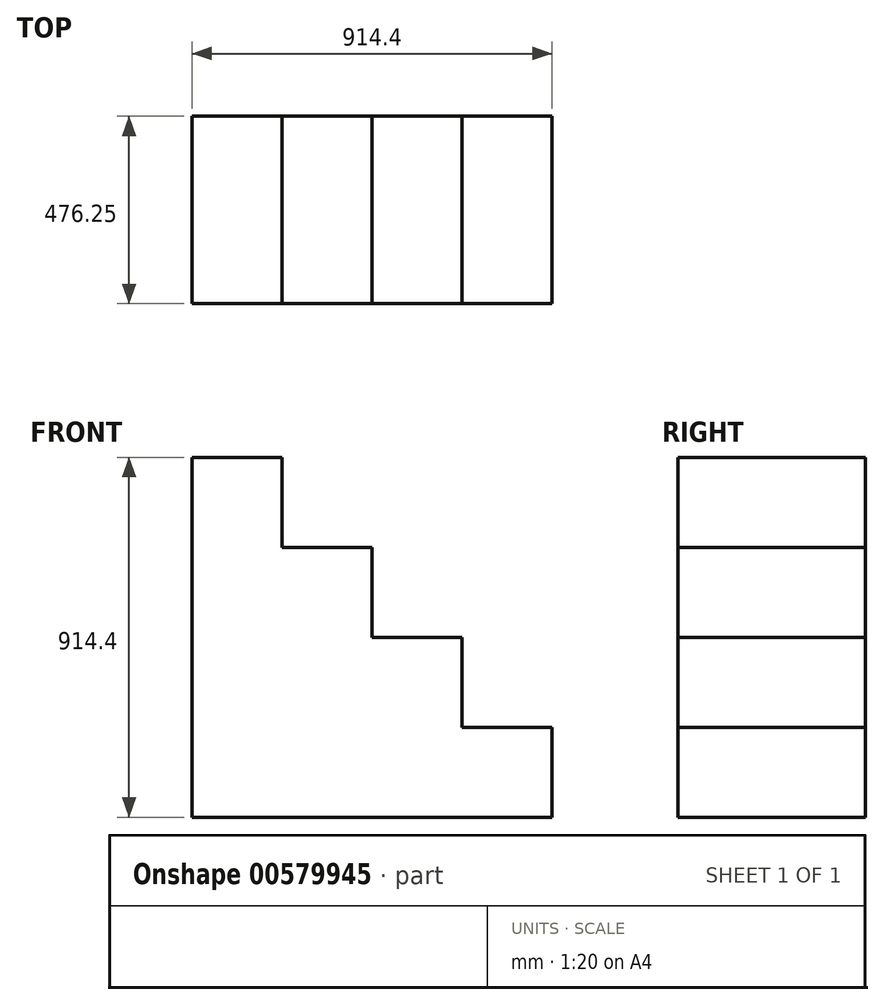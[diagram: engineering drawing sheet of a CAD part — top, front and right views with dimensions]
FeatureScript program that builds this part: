
annotation { "Feature Type Name" : "Feature", "Feature Type Description" : "" }
export const myFeature = defineFeature(function(context is Context, id is Id, definition is map)
    precondition{}
    {
        {
            var Q0;
            Q0=qCreatedBy(makeId("Right.planeOp"),FACE);
            var sketch = newSketch(context, id + "F0", { "sketchPlane" : qUnion([Q0])});
            skLineSegment(sketch, "E0.bottom", {"start": v(-256.35, 550.9) * mm, "end": v(219.9, 550.9) * mm});
            skLineSegment(sketch, "E0.top", {"start": v(-256.35, -363.5) * mm, "end": v(219.9, -363.5) * mm});
            skLineSegment(sketch, "E0.left", {"start": v(-256.35, 550.9) * mm, "end": v(-256.35, -363.5) * mm});
            skLineSegment(sketch, "E0.right", {"start": v(219.9, 550.9) * mm, "end": v(219.9, -363.5) * mm});
            skSolve(sketch);
        }
        {
            var Q0;
            Q0=makeQuery(id+"F0.imprint","IMPRINT",FACE,{"disambiguationData":[TD([[makeQuery(id+"F0.imprint","IMPRINT",EDGE,{"derivedFrom":sQuery(id+"F0.wireOp",EDGE,"E0.bottom")}),-1.0]])]});
            extrude(context, id + "F1", {"entities" : qUnion([Q0]), "depth" : 228.6 * mm, "offsetDistance" : 25.4 * mm});
        }
        {
            var Q0;
            Q0=makeQuery(id+"F1.opExtrude","CAP_FACE",FACE,{"disambiguationData":[OSD([sQuery(id+"F0.wireOp",EDGE,"E0.bottom"),sQuery(id+"F0.wireOp",EDGE,"E0.top"),sQuery(id+"F0.wireOp",EDGE,"E0.left"),sQuery(id+"F0.wireOp",EDGE,"E0.right")])],"isStart":false});
            var sketch = newSketch(context, id + "F2", { "sketchPlane" : qUnion([Q0])});
            skLineSegment(sketch, "E1.bottom", {"start": v(-256.35, -363.5) * mm, "end": v(219.9, -363.5) * mm});
            skLineSegment(sketch, "E1.top", {"start": v(-256.35, 322.3) * mm, "end": v(219.9, 322.3) * mm});
            skLineSegment(sketch, "E1.left", {"start": v(-256.35, -363.5) * mm, "end": v(-256.35, 322.3) * mm});
            skLineSegment(sketch, "E1.right", {"start": v(219.9, -363.5) * mm, "end": v(219.9, 322.3) * mm});
            skSolve(sketch);
        }
        {
            var Q0;
            Q0=makeQuery(id+"F2.imprint","IMPRINT",FACE,{"disambiguationData":[TD([[makeQuery(id+"F2.imprint","IMPRINT",EDGE,{"derivedFrom":sQuery(id+"F2.wireOp",EDGE,"E1.bottom")}),1.0]])]});
            extrude(context, id + "F3", {"entities" : qUnion([Q0]), "operationType" : NewBodyOperationType.ADD, "depth" : 228.6 * mm, "offsetDistance" : 25.4 * mm});
        }
        {
            var Q0;
            Q0=makeQuery(id+"F3.opExtrude","CAP_FACE",FACE,{"disambiguationData":[OSD([sQuery(id+"F2.wireOp",EDGE,"E1.bottom"),sQuery(id+"F2.wireOp",EDGE,"E1.top"),sQuery(id+"F2.wireOp",EDGE,"E1.left"),sQuery(id+"F2.wireOp",EDGE,"E1.right")])],"isStart":false});
            var sketch = newSketch(context, id + "F4", { "sketchPlane" : qUnion([Q0])});
            skLineSegment(sketch, "E2.bottom", {"start": v(-256.35, -363.5) * mm, "end": v(219.9, -363.5) * mm});
            skLineSegment(sketch, "E2.top", {"start": v(-256.35, 93.7) * mm, "end": v(219.9, 93.7) * mm});
            skLineSegment(sketch, "E2.left", {"start": v(-256.35, -363.5) * mm, "end": v(-256.35, 93.7) * mm});
            skLineSegment(sketch, "E2.right", {"start": v(219.9, -363.5) * mm, "end": v(219.9, 93.7) * mm});
            skSolve(sketch);
        }
        {
            var Q0;
            Q0=makeQuery(id+"F4.imprint","IMPRINT",FACE,{"disambiguationData":[TD([[makeQuery(id+"F4.imprint","IMPRINT",EDGE,{"derivedFrom":sQuery(id+"F4.wireOp",EDGE,"E2.bottom")}),1.0]])]});
            extrude(context, id + "F5", {"entities" : qUnion([Q0]), "operationType" : NewBodyOperationType.ADD, "depth" : 228.6 * mm, "offsetDistance" : 25.4 * mm});
        }
        {
            var Q0;
            Q0=makeQuery(id+"F5.opExtrude","CAP_FACE",FACE,{"disambiguationData":[OSD([sQuery(id+"F4.wireOp",EDGE,"E2.bottom"),sQuery(id+"F4.wireOp",EDGE,"E2.top"),sQuery(id+"F4.wireOp",EDGE,"E2.left"),sQuery(id+"F4.wireOp",EDGE,"E2.right")])],"isStart":false});
            var sketch = newSketch(context, id + "F6", { "sketchPlane" : qUnion([Q0])});
            skLineSegment(sketch, "E3.bottom", {"start": v(-256.35, -363.5) * mm, "end": v(219.9, -363.5) * mm});
            skLineSegment(sketch, "E3.top", {"start": v(-256.35, -134.9) * mm, "end": v(219.9, -134.9) * mm});
            skLineSegment(sketch, "E3.left", {"start": v(-256.35, -363.5) * mm, "end": v(-256.35, -134.9) * mm});
            skLineSegment(sketch, "E3.right", {"start": v(219.9, -363.5) * mm, "end": v(219.9, -134.9) * mm});
            skSolve(sketch);
        }
        {
            var Q0;
            Q0 = qSketchRegion(id + "F6", true);
            extrude(context, id + "F7", {"entities" : qUnion([Q0]), "operationType" : NewBodyOperationType.ADD, "depth" : 228.6 * mm, "offsetDistance" : 25.4 * mm});
        }
    });
